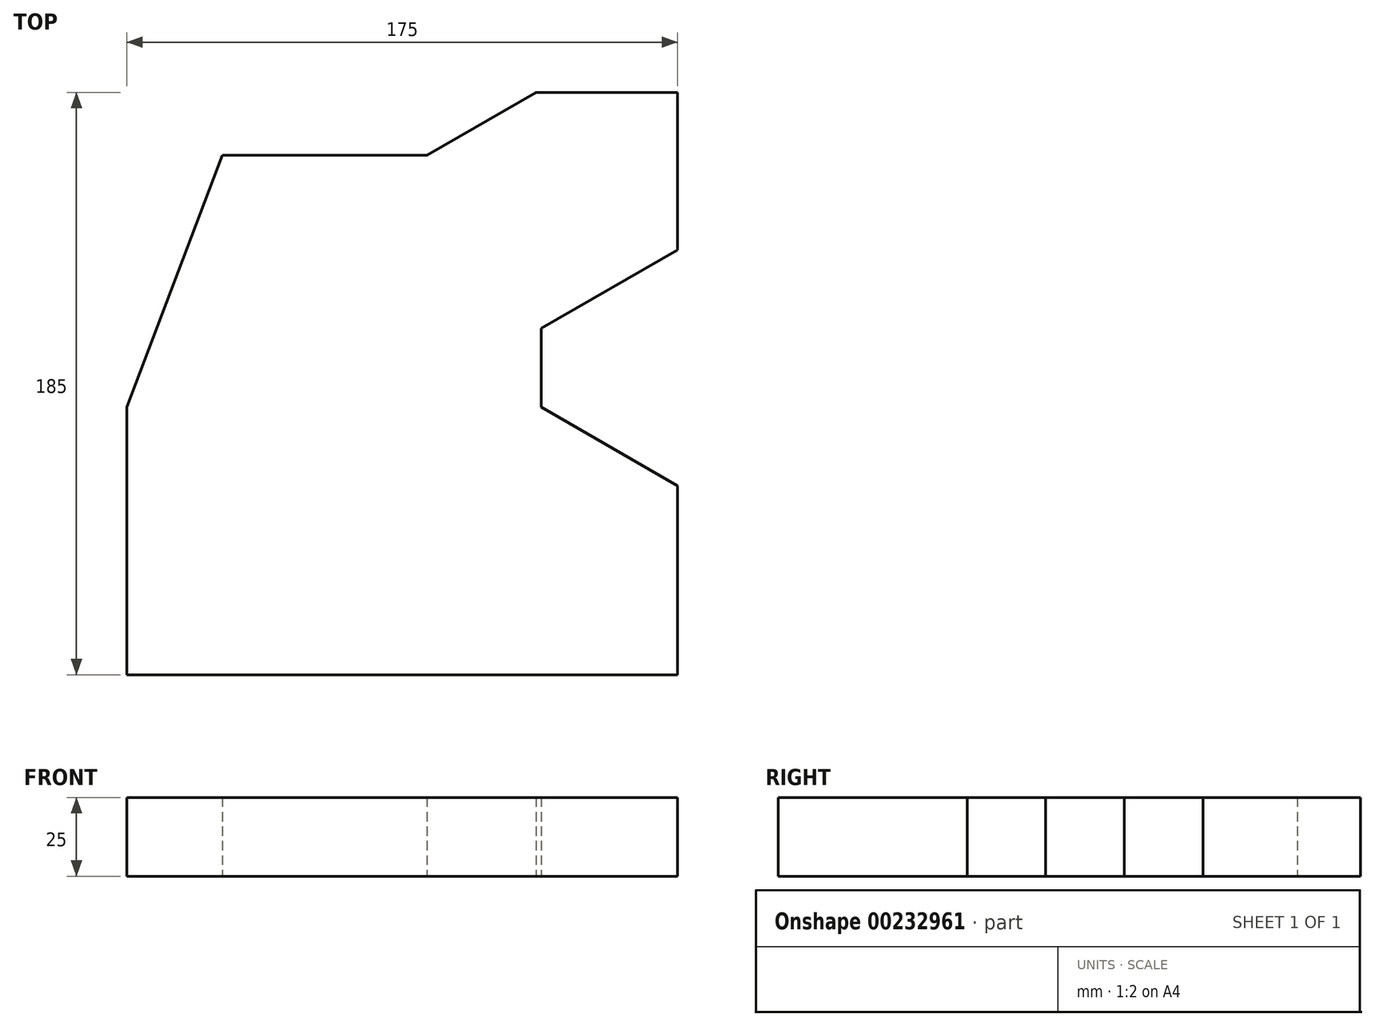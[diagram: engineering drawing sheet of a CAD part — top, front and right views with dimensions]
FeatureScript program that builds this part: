
annotation { "Feature Type Name" : "Feature", "Feature Type Description" : "" }
export const myFeature = defineFeature(function(context is Context, id is Id, definition is map)
    precondition{}
    {
        {
            var Q0;
            Q0=qCreatedBy(makeId("Top.planeOp"),FACE);
            var sketch = newSketch(context, id + "F0", { "sketchPlane" : qUnion([Q0])});
            skLineSegment(sketch, "E0", {"start": v(-92.85, -48.7) * mm, "end": v(82.15, -48.7) * mm});
            skLineSegment(sketch, "E1", {"start": v(-92.85, -48.7) * mm, "end": v(-92.85, 36.3) * mm});
            skLineSegment(sketch, "E2", {"start": v(82.15, -48.7) * mm, "end": v(82.15, 11.3) * mm});
            skLineSegment(sketch, "E3", {"start": v(82.15, 11.3) * mm, "end": v(38.85, 36.3) * mm});
            skLineSegment(sketch, "E4", {"start": v(38.85, 36.3) * mm, "end": v(119.22, 36.3) * mm});
            skLineSegment(sketch, "E5", {"start": v(38.85, 36.3) * mm, "end": v(38.85, 61.3) * mm});
            skLineSegment(sketch, "E6", {"start": v(38.85, 61.3) * mm, "end": v(118.33, 61.3) * mm});
            skLineSegment(sketch, "E7", {"start": v(38.85, 61.3) * mm, "end": v(82.15, 86.3) * mm});
            skLineSegment(sketch, "E8", {"start": v(82.15, 86.3) * mm, "end": v(82.15, 136.3) * mm});
            skLineSegment(sketch, "E9", {"start": v(82.15, 136.3) * mm, "end": v(37.15, 136.3) * mm});
            skLineSegment(sketch, "E10", {"start": v(37.15, 136.3) * mm, "end": v(2.5, 116.3) * mm});
            skLineSegment(sketch, "E11", {"start": v(2.5, 116.3) * mm, "end": v(-62.5, 116.3) * mm});
            skLineSegment(sketch, "E12", {"start": v(-62.5, 116.3) * mm, "end": v(-92.85, 36.3) * mm});
            skSolve(sketch);
        }
        {
            var Q0;
            Q0=makeQuery(id+"F0.imprint","IMPRINT",FACE,{"disambiguationData":[TD([[makeQuery(id+"F0.imprint","IMPRINT",EDGE,{"derivedFrom":sQuery(id+"F0.wireOp",EDGE,"E0")}),1.0]])]});
            extrude(context, id + "F1", {"entities" : qUnion([Q0]), "depth" : 25 * mm});
        }
    });
